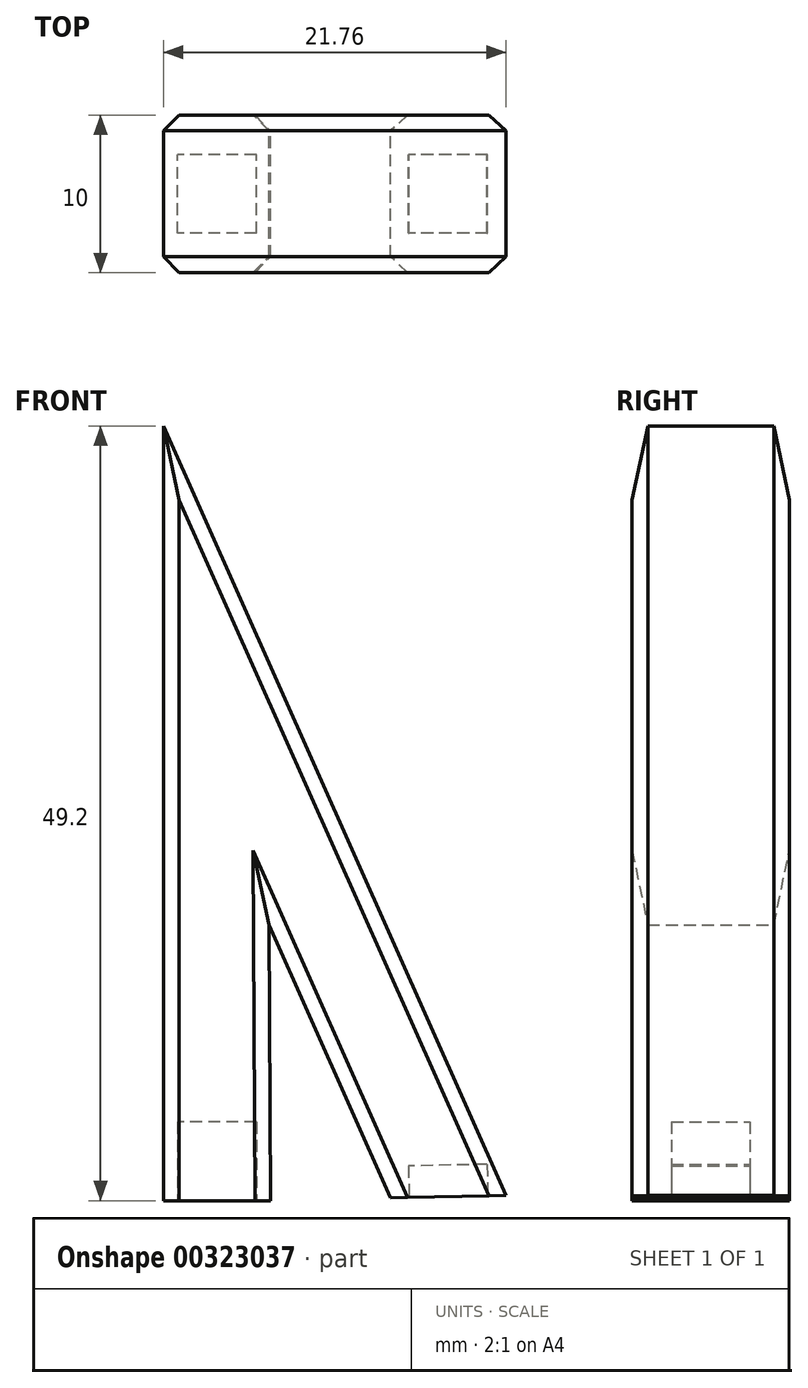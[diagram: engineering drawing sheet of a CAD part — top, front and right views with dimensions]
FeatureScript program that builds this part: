
annotation { "Feature Type Name" : "Feature", "Feature Type Description" : "" }
export const myFeature = defineFeature(function(context is Context, id is Id, definition is map)
    precondition{}
    {
        {
            var Q0;
            Q0=qCreatedBy(makeId("Front.planeOp"),FACE);
            var sketch = newSketch(context, id + "F0", { "sketchPlane" : qUnion([Q0])});
            skLineSegment(sketch, "E0", {"start": v(0, 0) * mm, "end": v(0, -49.2) * mm});
            skLineSegment(sketch, "E1", {"start": v(0, 0) * mm, "end": v(21.76, -48.87) * mm});
            skLineSegment(sketch, "E2", {"start": v(6.8, -49.2) * mm, "end": v(0, -49.2) * mm});
            skLineSegment(sketch, "E3", {"start": v(6.72, -31.7) * mm, "end": v(6.8, -49.2) * mm});
            skLineSegment(sketch, "E4", {"start": v(6.72, -31.7) * mm, "end": v(14.43, -49.01) * mm});
            skLineSegment(sketch, "E5", {"start": v(21.76, -48.87) * mm, "end": v(14.43, -49.01) * mm});
            skSolve(sketch);
        }
        {
            var Q0;
            Q0=makeQuery(id+"F0.imprint","IMPRINT",FACE,{"disambiguationData":[TD([[makeQuery(id+"F0.imprint","IMPRINT",EDGE,{"derivedFrom":sQuery(id+"F0.wireOp",EDGE,"E0")}),1.0]])]});
            extrude(context, id + "F1", {"entities" : qUnion([Q0]), "depth" : 10 * mm});
        }
        {
            var Q0;
            Q0=makeQuery(id+"F1.opExtrude","SWEPT_FACE",FACE,{"disambiguationData":[OSD([sQuery(id+"F0.wireOp",EDGE,"E2")])]});
            var sketch = newSketch(context, id + "F2", { "sketchPlane" : qUnion([Q0])});
            skLineSegment(sketch, "E6.bottom", {"start": v(5.9, 7.5) * mm, "end": v(0.9, 7.5) * mm});
            skLineSegment(sketch, "E6.top", {"start": v(5.9, 2.5) * mm, "end": v(0.9, 2.5) * mm});
            skLineSegment(sketch, "E6.left", {"start": v(5.9, 7.5) * mm, "end": v(5.9, 2.5) * mm});
            skLineSegment(sketch, "E6.right", {"start": v(0.9, 7.5) * mm, "end": v(0.9, 2.5) * mm});
            skPoint(sketch, "E6.middle", {"position": v(3.4, 5) * mm});
            skSolve(sketch);
        }
        {
            var Q0;
            Q0=makeQuery(id+"F2.imprint","IMPRINT",FACE,{"disambiguationData":[TD([[makeQuery(id+"F2.imprint","IMPRINT",EDGE,{"derivedFrom":sQuery(id+"F2.wireOp",EDGE,"E6.bottom")}),1.0]])]});
            extrude(context, id + "F3", {"entities" : qUnion([Q0]), "operationType" : NewBodyOperationType.REMOVE, "oppositeDirection" : true, "depth" : 5 * mm});
        }
        {
            var Q0;
            Q0=makeQuery(id+"F1.opExtrude","SWEPT_FACE",FACE,{"disambiguationData":[OSD([sQuery(id+"F0.wireOp",EDGE,"E5")])]});
            var sketch = newSketch(context, id + "F4", { "sketchPlane" : qUnion([Q0])});
            skLineSegment(sketch, "E7.bottom", {"start": v(19.67, 7.5) * mm, "end": v(14.67, 7.5) * mm});
            skLineSegment(sketch, "E7.top", {"start": v(19.67, 2.5) * mm, "end": v(14.67, 2.5) * mm});
            skLineSegment(sketch, "E7.left", {"start": v(19.67, 7.5) * mm, "end": v(19.67, 2.5) * mm});
            skLineSegment(sketch, "E7.right", {"start": v(14.67, 7.5) * mm, "end": v(14.67, 2.5) * mm});
            skPoint(sketch, "E7.middle", {"position": v(17.17, 5) * mm});
            skSolve(sketch);
        }
        {
            var Q0;
            Q0=makeQuery(id+"F4.imprint","IMPRINT",FACE,{"disambiguationData":[TD([[makeQuery(id+"F4.imprint","IMPRINT",EDGE,{"derivedFrom":sQuery(id+"F4.wireOp",EDGE,"E7.bottom")}),1.0]])]});
            extrude(context, id + "F5", {"entities" : qUnion([Q0]), "operationType" : NewBodyOperationType.REMOVE, "oppositeDirection" : true, "depth" : 2 * mm});
        }
        {
            var Q0;
            Q0=makeQuery(id+"F1.opExtrude","CAP_EDGE",EDGE,{"disambiguationData":[OSD([sQuery(id+"F0.wireOp",EDGE,"E1")])],"isStart":false});
            var Q1;
            Q1=makeQuery(id+"F1.opExtrude","CAP_EDGE",EDGE,{"disambiguationData":[OSD([sQuery(id+"F0.wireOp",EDGE,"E4")])],"isStart":false});
            var Q2;
            Q2=makeQuery(id+"F1.opExtrude","CAP_EDGE",EDGE,{"disambiguationData":[OSD([sQuery(id+"F0.wireOp",EDGE,"E3")])],"isStart":true});
            var Q3;
            Q3=makeQuery(id+"F1.opExtrude","CAP_EDGE",EDGE,{"disambiguationData":[OSD([sQuery(id+"F0.wireOp",EDGE,"E3")])],"isStart":false});
            var Q4;
            Q4=makeQuery(id+"F1.opExtrude","CAP_EDGE",EDGE,{"disambiguationData":[OSD([sQuery(id+"F0.wireOp",EDGE,"E0")])],"isStart":false});
            var Q5;
            Q5=makeQuery(id+"F1.opExtrude","CAP_EDGE",EDGE,{"disambiguationData":[OSD([sQuery(id+"F0.wireOp",EDGE,"E0")])],"isStart":true});
            var Q6;
            Q6=makeQuery(id+"F1.opExtrude","CAP_EDGE",EDGE,{"disambiguationData":[OSD([sQuery(id+"F0.wireOp",EDGE,"E4")])],"isStart":true});
            var Q7;
            Q7=makeQuery(id+"F1.opExtrude","CAP_EDGE",EDGE,{"disambiguationData":[OSD([sQuery(id+"F0.wireOp",EDGE,"E1")])],"isStart":true});
            chamfer(context, id + "F6", {"entities" : qUnion([Q0, Q1, Q2, Q3, Q4, Q5, Q6, Q7]), "width" : 1 * mm, "tangentPropagation" : true});
        }
    });
